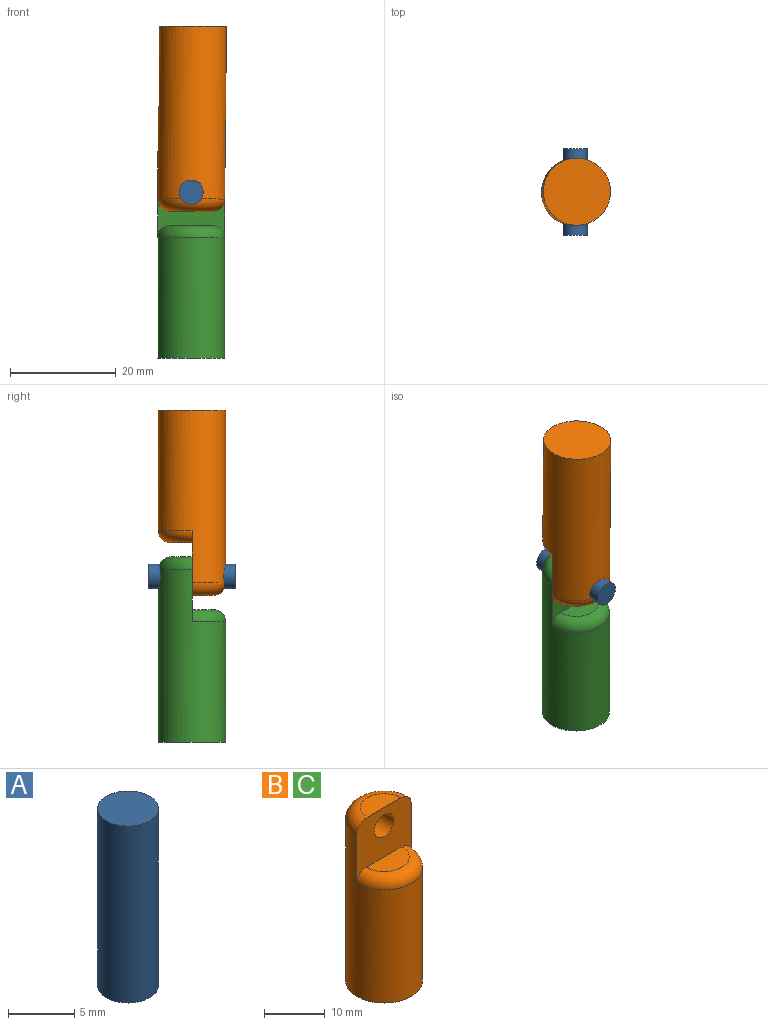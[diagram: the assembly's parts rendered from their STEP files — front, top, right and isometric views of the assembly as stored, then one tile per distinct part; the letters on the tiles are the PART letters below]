
ASSEMBLY  parts=3 mates=2
PART A: 3 faces, bbox 4.6x4.6x16.4 mm
  f0: cylinder r=2.3mm len=16.4mm, axis (0,0,-1), area 237mm2, adj f1,f2
  f1: plane 4.6x4.6mm, normal (0,0,1), area 16.6mm2, adj f0
  f2: plane 4.6x4.6mm, normal (0,0,-1), area 16.6mm2, adj f0
PART B: 8 faces, bbox 13.7x13.7x35 mm
  f0: cylinder r=6.35mm len=32.59mm, axis (0,0,-1), area 1092mm2, adj f1,f3,f4,f6,f7
  f1: plane 12.7x12.17mm, normal (0,-1,0), area 110.6mm2, adj f0,f2,f4,f5,f6,f7
  f2: plane 8.35x4.18mm, normal (0,0,1), area 27.4mm2, adj f1,f7
  f3: plane 12.7x12.7mm, normal (0,0,-1), area 126.7mm2, adj f0
  f4: cylinder r=2.25mm len=6.35mm, axis (0,-1,0), area 86.4mm2, adj f0,f1,f6
  f5: plane 7.87x3.94mm, normal (0,0,1), area 24.3mm2, adj f1,f6
  f6: torus R=3.94mm, axis (0,0,1), area 62.4mm2, adj f0,f1,f4,f5
  f7: torus R=4.18mm, axis (0,0,1), area 59.6mm2, adj f0,f1,f2
PART C: same geometry as B
PLACE A rot(axis=(-1,0,0),90deg) t=(-7.58,0.15,31.59)mm fixed
PLACE B rot(axis=(1,0,-0.01),180deg) t=(-7.25,8.35,62.94)mm
PLACE C t=(-7.58,8.35,0.24)mm
MATE revolute B.f4 <-> A.f0  axis (0,1,0) through (-7.58,8.35,31.59)mm
MATE revolute A.f0 <-> C.f4  axis (0,-1,0) through (-7.58,8.35,31.59)mm
